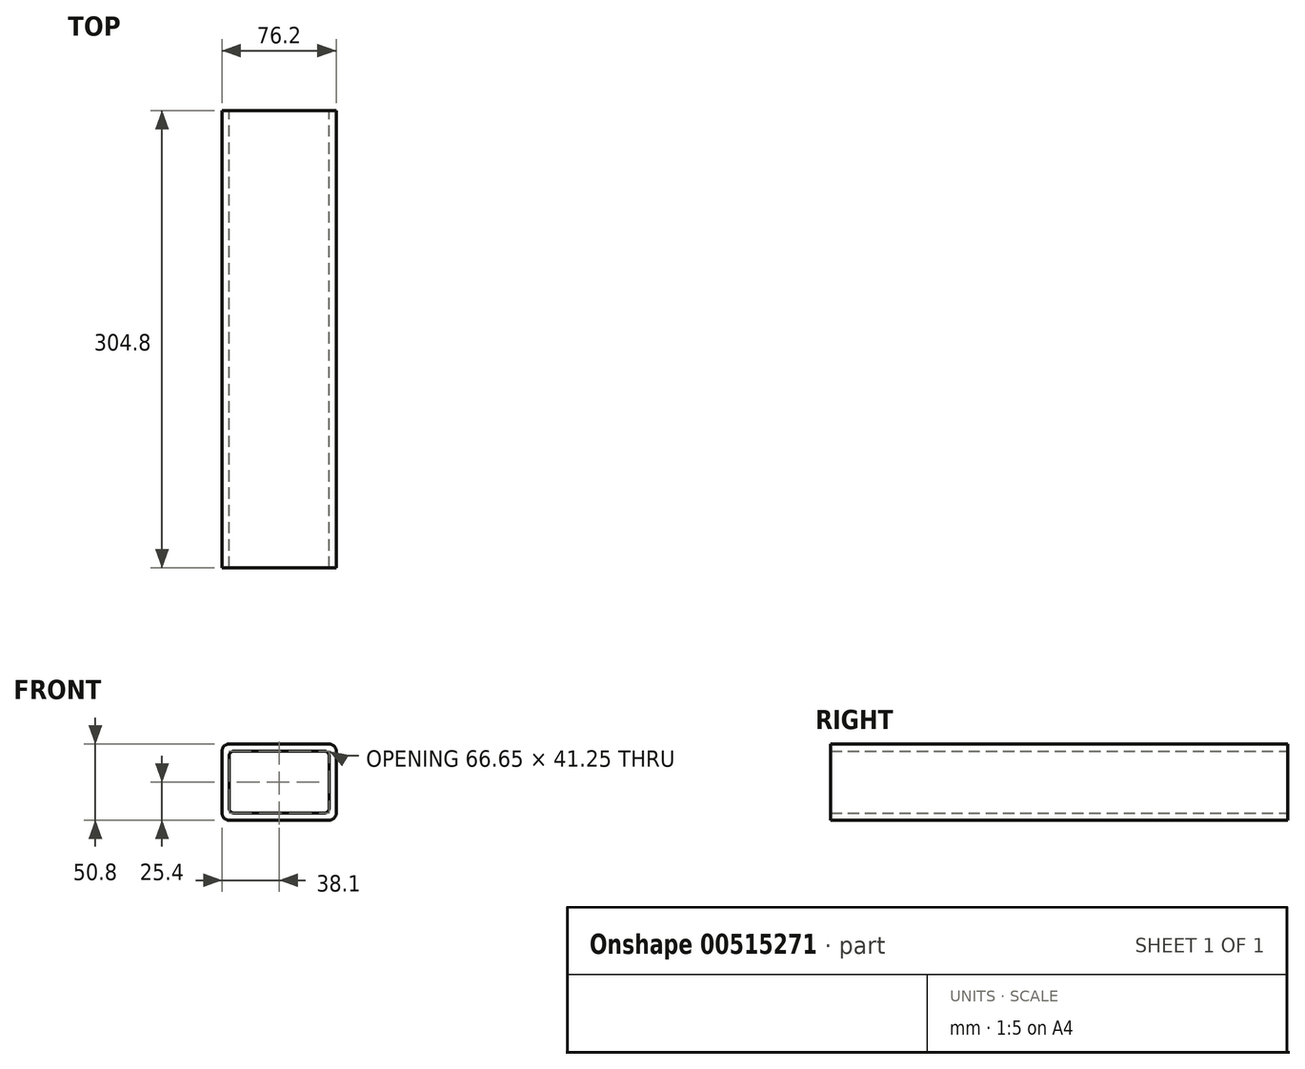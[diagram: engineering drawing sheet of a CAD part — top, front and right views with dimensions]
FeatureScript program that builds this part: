
annotation { "Feature Type Name" : "Feature", "Feature Type Description" : "" }
export const myFeature = defineFeature(function(context is Context, id is Id, definition is map)
    precondition{}
    {
        {
            var Q0;
            Q0=qCreatedBy(makeId("Front.planeOp"),FACE);
            var sketch = newSketch(context, id + "F0", { "sketchPlane" : qUnion([Q0])});
            skLineSegment(sketch, "E0.bottom", {"start": v(-38.1, 25.4) * mm, "end": v(38.1, 25.4) * mm});
            skLineSegment(sketch, "E0.top", {"start": v(-38.1, -25.4) * mm, "end": v(38.1, -25.4) * mm});
            skLineSegment(sketch, "E0.left", {"start": v(-38.1, 25.4) * mm, "end": v(-38.1, -25.4) * mm});
            skLineSegment(sketch, "E0.right", {"start": v(38.1, 25.4) * mm, "end": v(38.1, -25.4) * mm});
            skPoint(sketch, "E0.middle", {"position": v(0, 0) * mm});
            skLineSegment(sketch, "E1.0", {"start": v(33.32, 20.62) * mm, "end": v(33.32, -20.62) * mm});
            skLineSegment(sketch, "E1.1", {"start": v(-33.32, 20.62) * mm, "end": v(33.32, 20.62) * mm});
            skLineSegment(sketch, "E1.2", {"start": v(-33.32, 20.62) * mm, "end": v(-33.32, -20.62) * mm});
            skLineSegment(sketch, "E1.3", {"start": v(-33.32, -20.62) * mm, "end": v(33.32, -20.62) * mm});
            skSolve(sketch);
        }
        {
            var Q0;
            Q0 = qSketchRegion(id + "F0", true);
            extrude(context, id + "F1", {"entities" : qUnion([Q0]), "depth" : 304.8 * mm, "offsetDistance" : 25.4 * mm});
        }
        {
            var Q0;
            Q0=makeQuery(id+"F1.opExtrude","SWEPT_EDGE",EDGE,{"disambiguationData":[OSD([sQuery(id+"F0.wireOp",EDGE,"E0.top"),sQuery(id+"F0.wireOp",EDGE,"E0.right")])]});
            var Q1;
            Q1=makeQuery(id+"F1.opExtrude","SWEPT_EDGE",EDGE,{"disambiguationData":[OSD([sQuery(id+"F0.wireOp",EDGE,"E0.top"),sQuery(id+"F0.wireOp",EDGE,"E0.left")])]});
            var Q2;
            Q2=makeQuery(id+"F1.opExtrude","SWEPT_EDGE",EDGE,{"disambiguationData":[OSD([sQuery(id+"F0.wireOp",EDGE,"E0.bottom"),sQuery(id+"F0.wireOp",EDGE,"E0.left")])]});
            var Q3;
            Q3=makeQuery(id+"F1.opExtrude","SWEPT_EDGE",EDGE,{"disambiguationData":[OSD([sQuery(id+"F0.wireOp",EDGE,"E0.bottom"),sQuery(id+"F0.wireOp",EDGE,"E0.right")])]});
            fillet(context, id + "F2", {"entities" : qUnion([Q0, Q1, Q2, Q3]), "radius" : 4.78 * mm, "tangentPropagation" : true, "allowEdgeOverflow" : false});
        }
        {
            var Q0;
            Q0=makeQuery(id+"F1.opExtrude","SWEPT_EDGE",EDGE,{"disambiguationData":[OSD([sQuery(id+"F0.wireOp",EDGE,"E1.1"),sQuery(id+"F0.wireOp",EDGE,"E1.2")])]});
            var Q1;
            Q1=makeQuery(id+"F1.opExtrude","SWEPT_EDGE",EDGE,{"disambiguationData":[OSD([sQuery(id+"F0.wireOp",EDGE,"E1.0"),sQuery(id+"F0.wireOp",EDGE,"E1.1")])]});
            var Q2;
            Q2=makeQuery(id+"F1.opExtrude","SWEPT_EDGE",EDGE,{"disambiguationData":[OSD([sQuery(id+"F0.wireOp",EDGE,"E1.2"),sQuery(id+"F0.wireOp",EDGE,"E1.3")])]});
            var Q3;
            Q3=makeQuery(id+"F1.opExtrude","SWEPT_EDGE",EDGE,{"disambiguationData":[OSD([sQuery(id+"F0.wireOp",EDGE,"E1.0"),sQuery(id+"F0.wireOp",EDGE,"E1.3")])]});
            fillet(context, id + "F3", {"entities" : qUnion([Q0, Q1, Q2, Q3]), "radius" : 3.17 * mm, "tangentPropagation" : true, "allowEdgeOverflow" : false});
        }
    });
